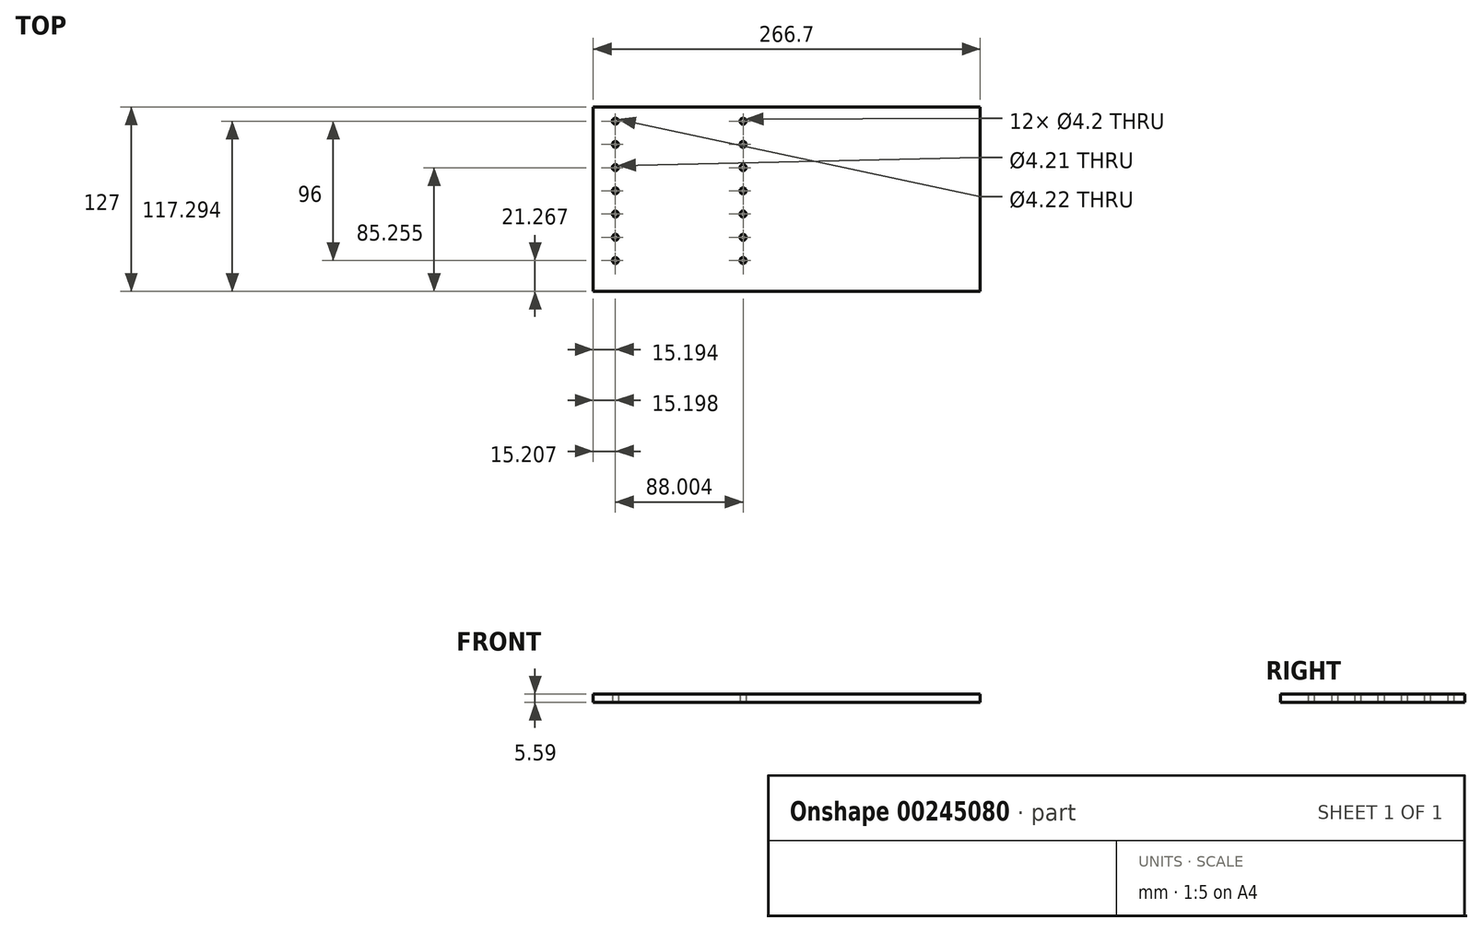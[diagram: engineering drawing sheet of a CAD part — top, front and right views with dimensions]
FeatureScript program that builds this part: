
annotation { "Feature Type Name" : "Feature", "Feature Type Description" : "" }
export const myFeature = defineFeature(function(context is Context, id is Id, definition is map)
    precondition{}
    {
        {
            var Q0;
            Q0=qCreatedBy(makeId("Top.planeOp"),FACE);
            var sketch = newSketch(context, id + "F0", { "sketchPlane" : qUnion([Q0])});
            skLineSegment(sketch, "E0.bottom", {"start": v(-178.52, 9.59) * mm, "end": v(88.18, 9.59) * mm});
            skLineSegment(sketch, "E0.top", {"start": v(-178.52, -117.41) * mm, "end": v(88.18, -117.41) * mm});
            skLineSegment(sketch, "E0.left", {"start": v(-178.52, 9.59) * mm, "end": v(-178.52, -117.41) * mm});
            skLineSegment(sketch, "E0.right", {"start": v(88.18, 9.59) * mm, "end": v(88.18, -117.41) * mm});
            skCircle(sketch, "E1", {"center": v(-163.32, -96.14) * mm, "radius": 2.1 * mm});
            skPoint(sketch, "E1.first.point", {"position": v(-163.35, -94.05) * mm});
            skPoint(sketch, "E1.second.point", {"position": v(-161.22, -96.17) * mm});
            skPoint(sketch, "E1.third.point", {"position": v(-163.76, -98.2) * mm});
            skCircle(sketch, "E2", {"center": v(-163.32, -80.14) * mm, "radius": 2.1 * mm});
            skPoint(sketch, "E2.first.point", {"position": v(-163.36, -78.05) * mm});
            skPoint(sketch, "E2.second.point", {"position": v(-161.3, -80.72) * mm});
            skPoint(sketch, "E2.third.point", {"position": v(-164.82, -81.62) * mm});
            skCircle(sketch, "E3", {"center": v(-163.31, -64.14) * mm, "radius": 2.1 * mm});
            skPoint(sketch, "E3.first.point", {"position": v(-163.33, -62.04) * mm});
            skPoint(sketch, "E3.second.point", {"position": v(-164.4, -62.35) * mm});
            skPoint(sketch, "E3.third.point", {"position": v(-162.47, -66.06) * mm});
            skCircle(sketch, "E4", {"center": v(-163.31, -48.15) * mm, "radius": 2.1 * mm});
            skPoint(sketch, "E4.first.point", {"position": v(-163.32, -46.05) * mm});
            skPoint(sketch, "E4.second.point", {"position": v(-164.57, -46.47) * mm});
            skPoint(sketch, "E4.third.point", {"position": v(-162.61, -50.12) * mm});
            skCircle(sketch, "E5", {"center": v(-163.33, -32.15) * mm, "radius": 2.1 * mm});
            skPoint(sketch, "E5.first.point", {"position": v(-164.4, -30.35) * mm});
            skPoint(sketch, "E5.second.point", {"position": v(-164.8, -30.66) * mm});
            skPoint(sketch, "E5.third.point", {"position": v(-162.2, -33.93) * mm});
            skCircle(sketch, "E6", {"center": v(-163.31, -16.14) * mm, "radius": 2.1 * mm});
            skPoint(sketch, "E6.first.point", {"position": v(-165, -14.89) * mm});
            skPoint(sketch, "E6.second.point", {"position": v(-165.24, -15.3) * mm});
            skPoint(sketch, "E6.third.point", {"position": v(-161.75, -17.54) * mm});
            skCircle(sketch, "E7", {"center": v(-163.31, -0.12) * mm, "radius": 2.11 * mm});
            skPoint(sketch, "E7.first.point", {"position": v(-165.38, -0.53) * mm});
            skPoint(sketch, "E7.second.point", {"position": v(-165.33, -0.74) * mm});
            skPoint(sketch, "E7.third.point", {"position": v(-161.42, -1.05) * mm});
            skCircle(sketch, "E8", {"center": v(-75.32, -0.14) * mm, "radius": 2.1 * mm});
            skPoint(sketch, "E8.first.point", {"position": v(-76.02, -2.12) * mm});
            skPoint(sketch, "E8.second.point", {"position": v(-74.5, -2.07) * mm});
            skPoint(sketch, "E8.third.point", {"position": v(-74.92, 1.92) * mm});
            skCircle(sketch, "E9", {"center": v(-75.32, -16.14) * mm, "radius": 2.1 * mm});
            skPoint(sketch, "E9.first.point", {"position": v(-74.98, -14.07) * mm});
            skPoint(sketch, "E9.second.point", {"position": v(-77.32, -16.76) * mm});
            skPoint(sketch, "E9.third.point", {"position": v(-74.8, -18.18) * mm});
            skCircle(sketch, "E10", {"center": v(-75.32, -32.14) * mm, "radius": 2.1 * mm});
            skPoint(sketch, "E10.first.point", {"position": v(-75.24, -34.24) * mm});
            skPoint(sketch, "E10.second.point", {"position": v(-74.35, -30.28) * mm});
            skPoint(sketch, "E10.third.point", {"position": v(-77.4, -31.94) * mm});
            skCircle(sketch, "E11", {"center": v(-75.32, -48.14) * mm, "radius": 2.1 * mm});
            skPoint(sketch, "E11.first.point", {"position": v(-75.04, -46.06) * mm});
            skPoint(sketch, "E11.second.point", {"position": v(-73.38, -47.34) * mm});
            skPoint(sketch, "E11.third.point", {"position": v(-76.99, -49.42) * mm});
            skCircle(sketch, "E12", {"center": v(-75.32, -64.14) * mm, "radius": 2.1 * mm});
            skPoint(sketch, "E12.first.point", {"position": v(-75.26, -62.04) * mm});
            skPoint(sketch, "E12.second.point", {"position": v(-73.26, -63.74) * mm});
            skPoint(sketch, "E12.third.point", {"position": v(-75.62, -66.22) * mm});
            skCircle(sketch, "E13", {"center": v(-75.32, -80.14) * mm, "radius": 2.1 * mm});
            skPoint(sketch, "E13.first.point", {"position": v(-74.2, -78.36) * mm});
            skPoint(sketch, "E13.second.point", {"position": v(-77.15, -79.13) * mm});
            skPoint(sketch, "E13.third.point", {"position": v(-74.72, -82.16) * mm});
            skCircle(sketch, "E14", {"center": v(-75.32, -96.14) * mm, "radius": 2.1 * mm});
            skPoint(sketch, "E14.first.point", {"position": v(-74.13, -94.41) * mm});
            skPoint(sketch, "E14.second.point", {"position": v(-77.4, -96.33) * mm});
            skPoint(sketch, "E14.third.point", {"position": v(-75.1, -98.23) * mm});
            skSolve(sketch);
        }
        {
            var Q0;
            Q0=makeQuery(id+"F0.imprint","IMPRINT",FACE,{"disambiguationData":[TD([[makeQuery(id+"F0.imprint","IMPRINT",EDGE,{"derivedFrom":sQuery(id+"F0.wireOp",EDGE,"E0.bottom")}),-1.0]])]});
            extrude(context, id + "F1", {"entities" : qUnion([Q0]), "depth" : 5.6 * mm});
        }
    });
